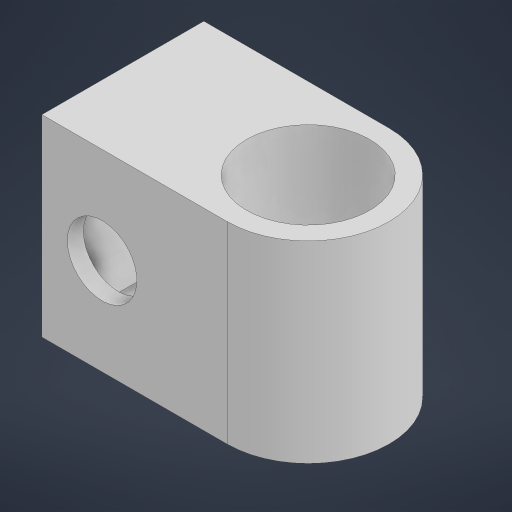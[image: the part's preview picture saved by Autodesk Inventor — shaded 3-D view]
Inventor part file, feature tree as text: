
AUTODESK INVENTOR PART (.ipt)
format: ipt  version: 2023 (Build 270158000, 158)  size: 189,952 bytes
history: native  units: mm
features: extrude x4, sketch x4
ambient origin geometry x8: Origin, YZ Plane, XZ Plane, XY Plane, X Axis, Y Axis, Z Axis, Center Point
bodies: Solid1 (feature_tree)
feature tree (8):
  extrude  "Extrusion1"  Depth=30.25mm
  extrude  "Extrusion2"  Depth=3.0mm
  extrude  "Extrusion3"  Depth=3.0mm
  extrude  "Extrusion4"  Depth=3.0mm TaperAngle=0.0deg
  sketch  "Sketch1"  dims[d0=23.0mm d1=30.25mm]
  sketch  "Sketch2"  dims[d2=36.0mm d3=0.0mm d4=3.0mm]
  sketch  "Sketch3"  dims[d5=3.0mm d6=3.0mm]
  sketch  "Sketch4"  dims[d7=16.5mm d8=0.0mm d9=3.0mm d10=0.0mm d11=13.0mm d12=3.0mm d13=0.0mm d14=0.5mm d15=0.872665mm d16=0.5mm d17=0.872665mm]
